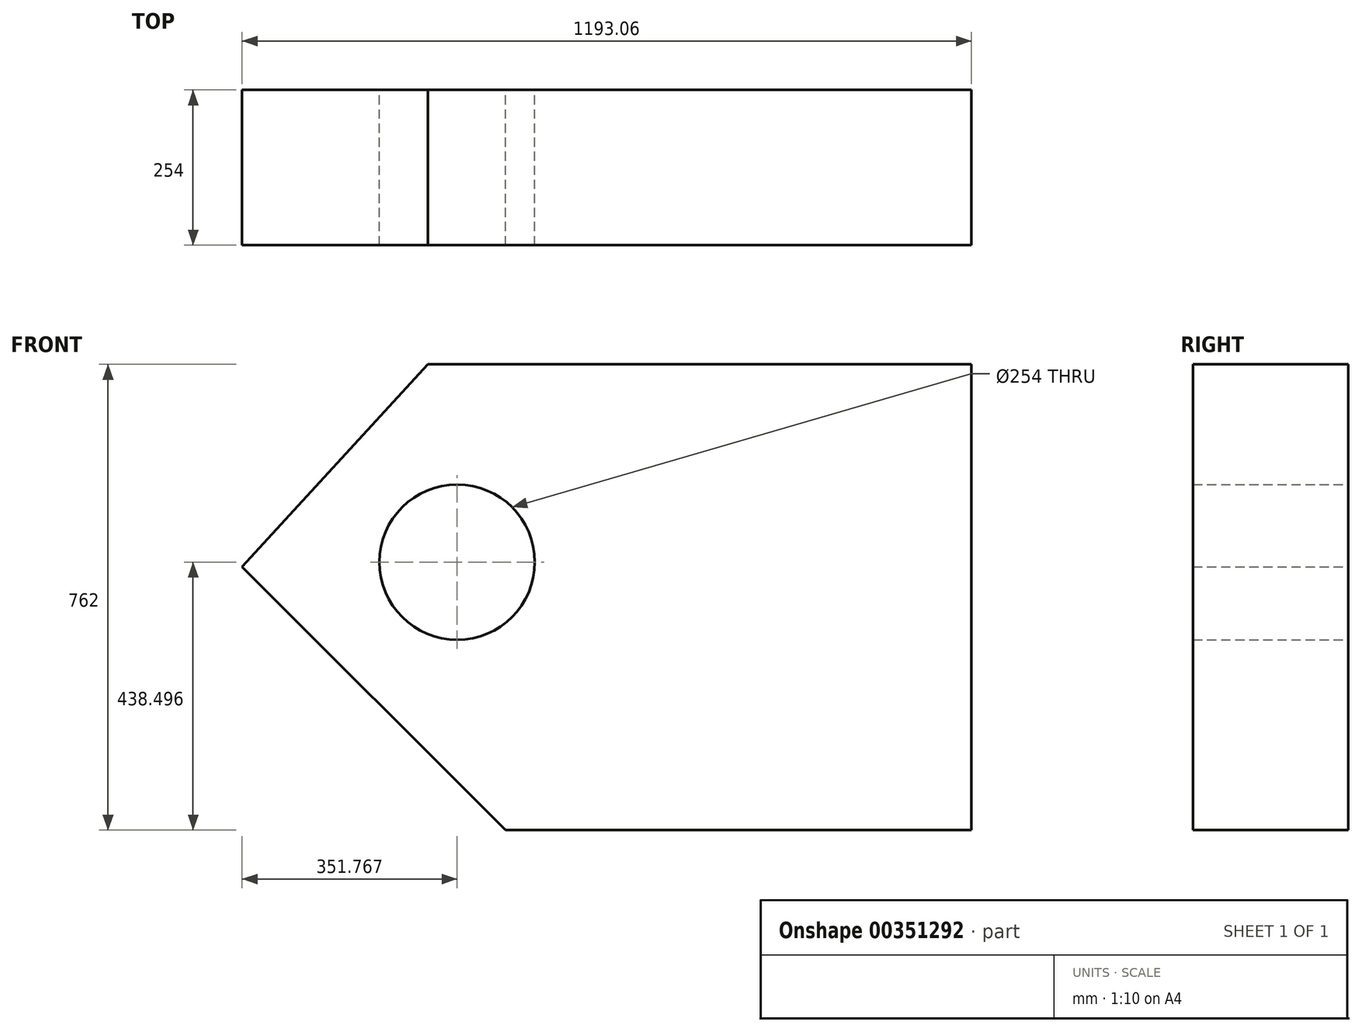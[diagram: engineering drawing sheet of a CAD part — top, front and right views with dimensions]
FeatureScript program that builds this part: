
annotation { "Feature Type Name" : "Feature", "Feature Type Description" : "" }
export const myFeature = defineFeature(function(context is Context, id is Id, definition is map)
    precondition{}
    {
        {
            var Q0;
            Q0=qCreatedBy(makeId("Front.planeOp"),FACE);
            var sketch = newSketch(context, id + "F0", { "sketchPlane" : qUnion([Q0])});
            skLineSegment(sketch, "E0", {"start": v(-1390.45, -431.05) * mm, "end": v(-628.45, -431.05) * mm});
            skLineSegment(sketch, "E1", {"start": v(-628.45, -431.05) * mm, "end": v(-628.45, 330.95) * mm});
            skLineSegment(sketch, "E2", {"start": v(-628.45, 330.95) * mm, "end": v(-1517.45, 330.95) * mm});
            skLineSegment(sketch, "E3", {"start": v(-1517.45, 330.95) * mm, "end": v(-1821.5, 0) * mm});
            skLineSegment(sketch, "E4", {"start": v(-1821.5, 0) * mm, "end": v(-1390.45, -431.05) * mm});
            skCircle(sketch, "E5", {"center": v(-1469.74, 7.45) * mm, "radius": 127 * mm});
            skSolve(sketch);
        }
        {
            var Q0;
            Q0=makeQuery(id+"F0.imprint","IMPRINT",FACE,{"disambiguationData":[TD([[makeQuery(id+"F0.imprint","IMPRINT",EDGE,{"derivedFrom":sQuery(id+"F0.wireOp",EDGE,"E0")}),1.0]])]});
            extrude(context, id + "F1", {"entities" : qUnion([Q0]), "depth" : 254 * mm});
        }
    });
